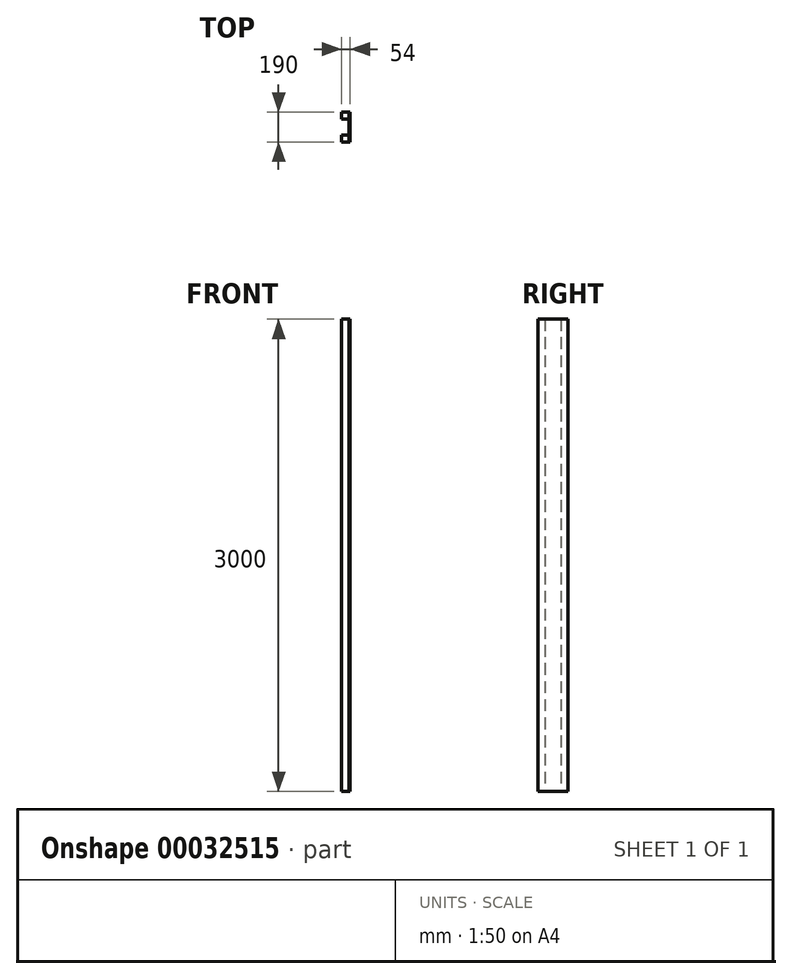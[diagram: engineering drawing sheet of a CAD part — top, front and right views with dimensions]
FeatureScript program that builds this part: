
annotation { "Feature Type Name" : "Feature", "Feature Type Description" : "" }
export const myFeature = defineFeature(function(context is Context, id is Id, definition is map)
    precondition{}
    {
        {
            var Q0;
            Q0=qCreatedBy(makeId("Top.planeOp"),FACE);
            var sketch = newSketch(context, id + "F0", { "sketchPlane" : qUnion([Q0])});
            skLineSegment(sketch, "E0.bottom", {"start": v(0, 0) * mm, "end": v(-9, 0) * mm});
            skLineSegment(sketch, "E0.top", {"start": v(0, 190) * mm, "end": v(-9, 190) * mm});
            skLineSegment(sketch, "E0.left", {"start": v(0, 0) * mm, "end": v(0, 190) * mm});
            skLineSegment(sketch, "E0.right", {"start": v(-9, 0) * mm, "end": v(-9, 190) * mm});
            skLineSegment(sketch, "E1.bottom", {"start": v(-9, 0) * mm, "end": v(-54, 0) * mm});
            skLineSegment(sketch, "E1.top", {"start": v(-9, 45) * mm, "end": v(-54, 45) * mm});
            skLineSegment(sketch, "E1.left", {"start": v(-9, 0) * mm, "end": v(-9, 45) * mm});
            skLineSegment(sketch, "E1.right", {"start": v(-54, 0) * mm, "end": v(-54, 45) * mm});
            skLineSegment(sketch, "E2.bottom", {"start": v(-9, 190) * mm, "end": v(-54, 190) * mm});
            skLineSegment(sketch, "E2.top", {"start": v(-9, 145) * mm, "end": v(-54, 145) * mm});
            skLineSegment(sketch, "E2.left", {"start": v(-9, 190) * mm, "end": v(-9, 145) * mm});
            skLineSegment(sketch, "E2.right", {"start": v(-54, 190) * mm, "end": v(-54, 145) * mm});
            skSolve(sketch);
        }
        {
            var Q0;
            Q0=makeQuery(id+"F0.imprint","IMPRINT",FACE,{"disambiguationData":[TD([[makeQuery(id+"F0.imprint","IMPRINT",EDGE,{"derivedFrom":sQuery(id+"F0.wireOp",EDGE,"E1.bottom")}),-1.0]])]});
            var Q1;
            Q1=makeQuery(id+"F0.imprint","IMPRINT",FACE,{"disambiguationData":[TD([[makeQuery(id+"F0.imprint","IMPRINT",EDGE,{"derivedFrom":sQuery(id+"F0.wireOp",EDGE,"E2.bottom")}),1.0]])]});
            extrude(context, id + "F1", {"entities" : qUnion([Q0, Q1]), "depth" : 3000 * mm});
        }
        {
            var Q0;
            Q0=makeQuery(id+"F0.imprint","IMPRINT",FACE,{"disambiguationData":[TD([[makeQuery(id+"F0.imprint","IMPRINT",EDGE,{"derivedFrom":sQuery(id+"F0.wireOp",EDGE,"E0.bottom")}),-1.0]])]});
            extrude(context, id + "F2", {"entities" : qUnion([Q0]), "depth" : 3000 * mm});
        }
    });
